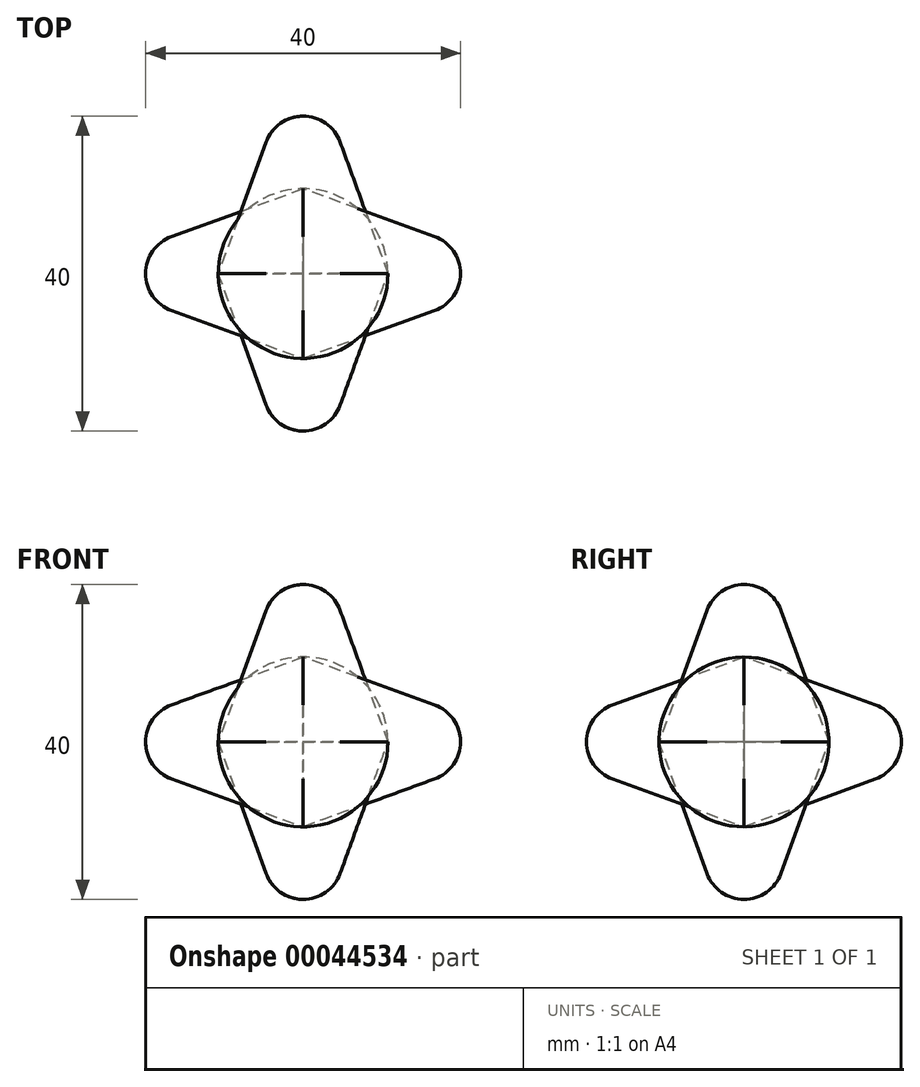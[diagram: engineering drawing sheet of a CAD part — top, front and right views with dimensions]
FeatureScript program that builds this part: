
annotation { "Feature Type Name" : "Feature", "Feature Type Description" : "" }
export const myFeature = defineFeature(function(context is Context, id is Id, definition is map)
    precondition{}
    {
        {
            var Q0;
            Q0=qCreatedBy(makeId("Front.planeOp"),FACE);
            var sketch = newSketch(context, id + "F0", { "sketchPlane" : qUnion([Q0])});
            skLineSegment(sketch, "E0", {"start": v(0, 0) * mm, "end": v(0, 15) * mm, "construction": true});
            skArc(sketch, "E1", {"start": v(0, 20) * mm, "mid": v(-2.87, 19.1) * mm, "end": v(-4.7, 16.71) * mm});
            skLineSegment(sketch, "E2", {"start": v(0, 20) * mm, "end": v(0, 0) * mm});
            skLineSegment(sketch, "E3", {"start": v(-10.78, 0) * mm, "end": v(-4.7, 16.71) * mm});
            skLineSegment(sketch, "E4", {"start": v(-10.78, 0) * mm, "end": v(0, 0) * mm});
            skSolve(sketch);
        }
        {
            var Q0;
            Q0=makeQuery(id+"F0.imprint","IMPRINT",FACE,{"disambiguationData":[TD([[makeQuery(id+"F0.imprint","IMPRINT",EDGE,{"derivedFrom":sQuery(id+"F0.wireOp",EDGE,"E1")}),1.0]])]});
            var Q1;
            Q1=sQuery(id+"F0.wireOp",EDGE,"E2");
            revolve(context, id + "F1", {"entities" : qUnion([Q0]), "axis" : qUnion([Q1]), "revolveType" : RevolveType.FULL});
        }
        {
            var Q0;
            Q0=qCreatedBy(makeId("Top.planeOp"),FACE);
            var sketch = newSketch(context, id + "F2", { "sketchPlane" : qUnion([Q0])});
            skLineSegment(sketch, "E5", {"start": v(0, 0) * mm, "end": v(45.16, 0) * mm});
            skLineSegment(sketch, "E6", {"start": v(0, 0) * mm, "end": v(0, -26.87) * mm});
            skSolve(sketch);
        }
        {
            var Q0;
            Q0=makeQuery(id+"F1.opRevolve","SWEPT_BODY",BODY,{"disambiguationData":[OSD([sQuery(id+"F0.wireOp",EDGE,"E1"),sQuery(id+"F0.wireOp",EDGE,"E2"),sQuery(id+"F0.wireOp",EDGE,"E3"),sQuery(id+"F0.wireOp",EDGE,"E4")])]});
            var Q1;
            Q1=sQuery(id+"F2.wireOp",EDGE,"E5");
            var Q2;
            Q2=sQuery(id+"F2.wireOp",EDGE,"E6");
            transform(context, id + "F3", {"entities" : qUnion([Q0]), "transformType" : TransformType.ROTATION, "transformAxis" : qUnion([Q2]), "angle" : 90 * degree, "makeCopy" : true});
        }
        {
            var Q0;
            Q0=makeQuery(id+"F1.opRevolve","SWEPT_BODY",BODY,{"disambiguationData":[OSD([sQuery(id+"F0.wireOp",EDGE,"E1"),sQuery(id+"F0.wireOp",EDGE,"E2"),sQuery(id+"F0.wireOp",EDGE,"E3"),sQuery(id+"F0.wireOp",EDGE,"E4")])]});
            var Q1;
            Q1=sQuery(id+"F2.wireOp",EDGE,"E6");
            transform(context, id + "F4", {"entities" : qUnion([Q0]), "transformType" : TransformType.ROTATION, "transformAxis" : qUnion([Q1]), "angle" : 90 * degree, "oppositeDirection" : true, "makeCopy" : true});
        }
        {
            var Q0;
            Q0=makeQuery(id+"F1.opRevolve","SWEPT_BODY",BODY,{"disambiguationData":[OSD([sQuery(id+"F0.wireOp",EDGE,"E1"),sQuery(id+"F0.wireOp",EDGE,"E2"),sQuery(id+"F0.wireOp",EDGE,"E3"),sQuery(id+"F0.wireOp",EDGE,"E4")])]});
            var Q1;
            Q1=sQuery(id+"F2.wireOp",EDGE,"E5");
            circularPattern(context, id + "F5", {"entities" : qUnion([Q0]), "axis" : qUnion([Q1]), "angle" : 360 * degree, "instanceCount" : 4, "equalSpace" : true});
        }
    });
